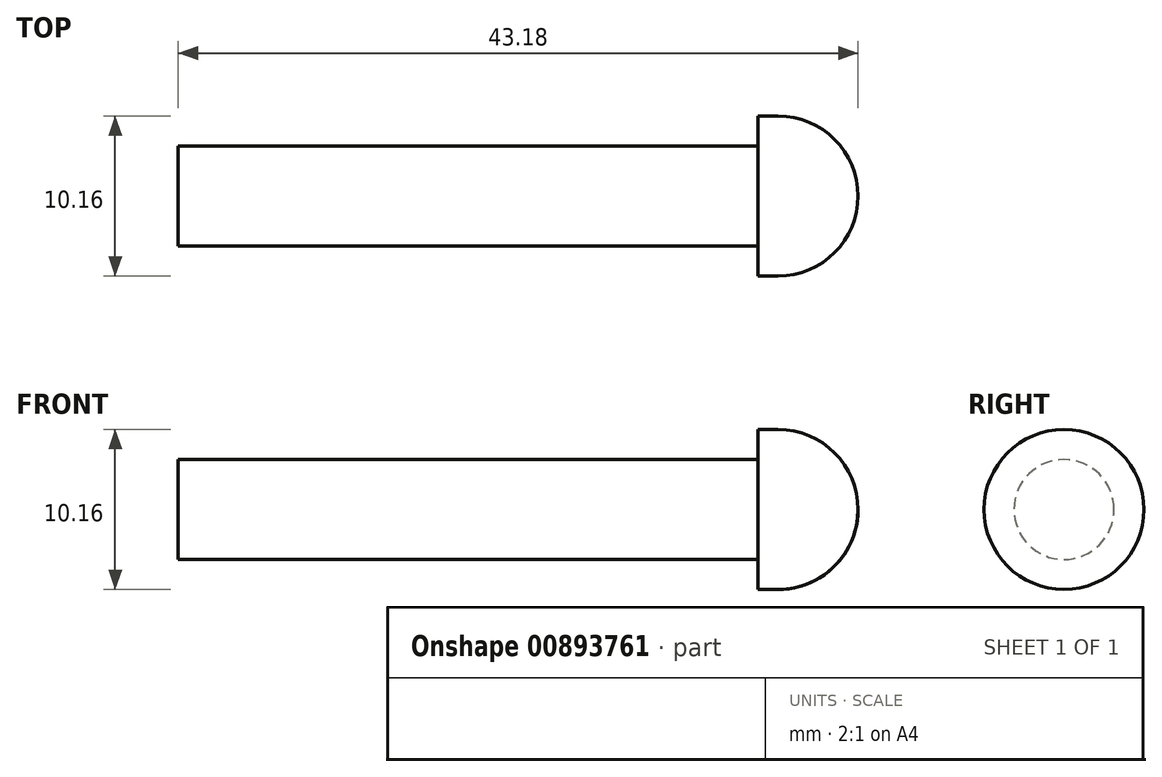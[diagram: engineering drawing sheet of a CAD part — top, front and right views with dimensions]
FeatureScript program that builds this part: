
annotation { "Feature Type Name" : "Feature", "Feature Type Description" : "" }
export const myFeature = defineFeature(function(context is Context, id is Id, definition is map)
    precondition{}
    {
        {
            var Q0;
            Q0=qCreatedBy(makeId("Right.planeOp"),FACE);
            var sketch = newSketch(context, id + "F0", { "sketchPlane" : qUnion([Q0])});
            skCircle(sketch, "E0", {"center": v(0, 0) * mm, "radius": 3.18 * mm});
            skSolve(sketch);
        }
        {
            var Q0;
            Q0=qSketchRegion(id+"F0",true);
            extrude(context, id + "F1", {"entities" : qUnion([Q0]), "depth" : 36.83 * mm, "offsetDistance" : 25.4 * mm});
        }
        {
            var Q0;
            Q0=makeQuery(id+"F1.opExtrude","CAP_FACE",FACE,{"disambiguationData":[OSD([sQuery(id+"F0.wireOp",EDGE,"E0")])],"isStart":false});
            var sketch = newSketch(context, id + "F2", { "sketchPlane" : qUnion([Q0])});
            skCircle(sketch, "E1", {"center": v(0, 0) * mm, "radius": 5.08 * mm});
            skSolve(sketch);
        }
        {
            var Q0;
            Q0=qSketchRegion(id+"F2",true);
            extrude(context, id + "F3", {"entities" : qUnion([Q0]), "operationType" : NewBodyOperationType.ADD, "depth" : 6.35 * mm, "offsetDistance" : 25.4 * mm});
        }
        {
            var Q0;
            Q0=makeQuery(id+"F3.opExtrude","CAP_EDGE",EDGE,{"disambiguationData":[OSD([sQuery(id+"F2.wireOp",EDGE,"E1")])],"isStart":false});
            fillet(context, id + "F4", {"entities" : qUnion([Q0]), "radius" : 5.08 * mm, "tangentPropagation" : true, "allowEdgeOverflow" : false});
        }
    });
